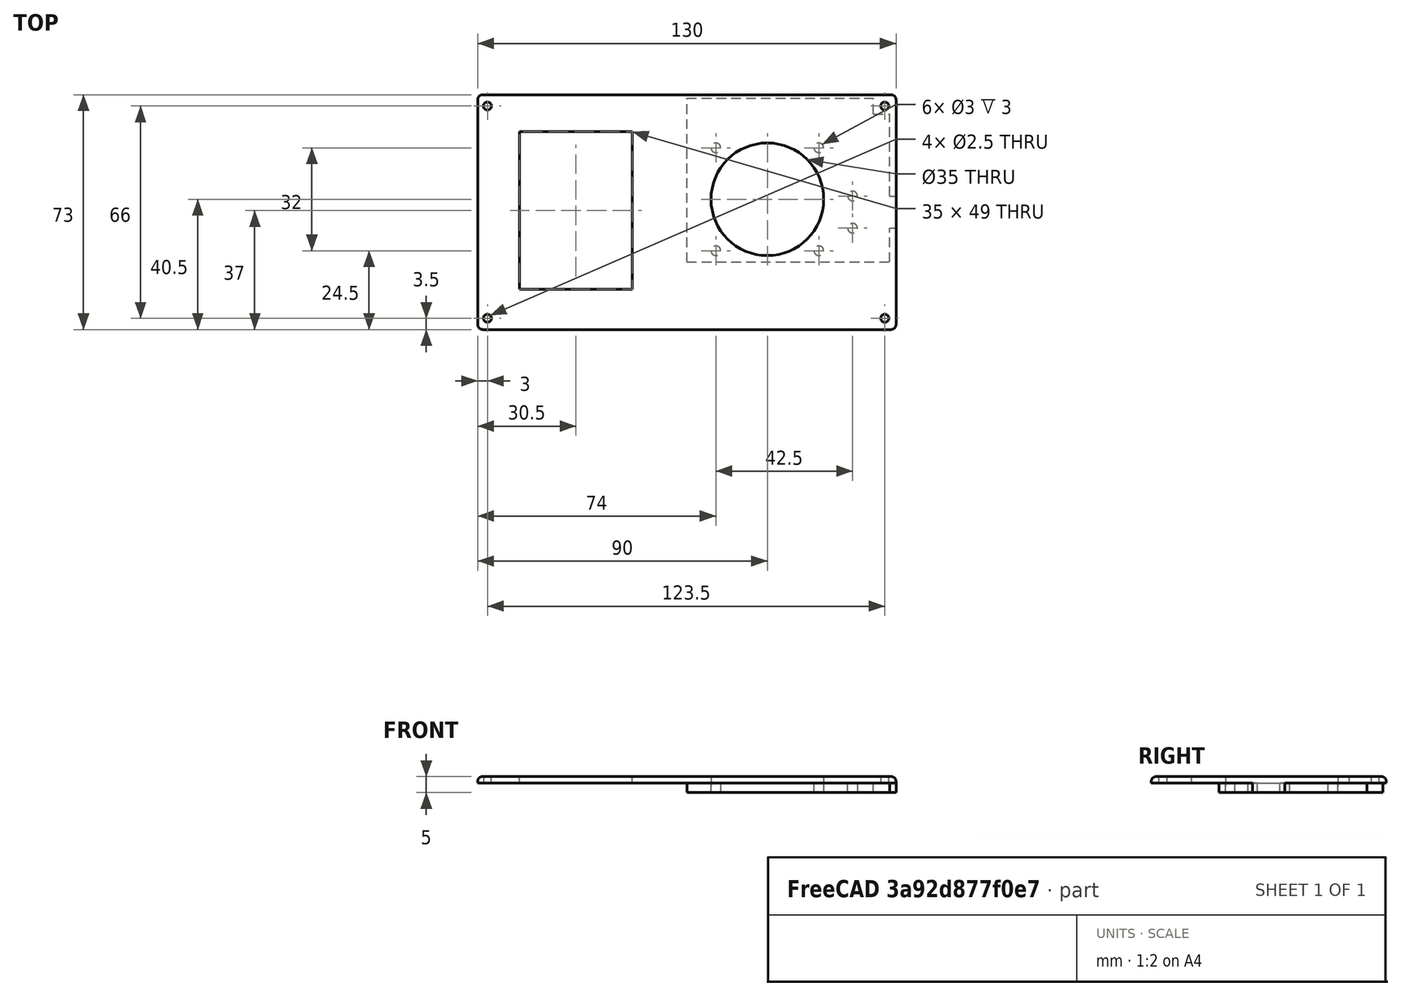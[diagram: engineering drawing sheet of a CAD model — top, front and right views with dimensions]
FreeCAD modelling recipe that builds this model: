
FCSTD DOCUMENT  (FreeCAD 1.0R39285 (Git))
Label: caseTop
License: All rights reserved
LicenseURL: https://en.wikipedia.org/wiki/All_rights_reserved
objects: PartDesign::SubtractiveCylinder×12, PartDesign::Fillet×4, PartDesign::AdditiveBox×3, PartDesign::SubtractiveBox×2, PartDesign::Body×1
note: 64 computed .brp shape members not serialized (recipe doc carries the construction recipe); baked Part::Feature solids carry a one-line shape summary decoded from their .brp

FEATURE [PartDesign::AdditiveBox] Box  label="base"
  AttacherType = Attacher::AttachEngine3D
  Height = 2
  Length = 130
  Refine = true
  Suppressed = false
  Width = 73
FEATURE [PartDesign::SubtractiveBox] Box001  label="screen"
  AttacherType = Attacher::AttachEngine3D
  AttachmentOffset = pos=(13,12.5,-4) rot=(0,0,1;0rad)
  AttachmentSupport = -> [Box]
  BaseFeature = -> Box
  Height = 4
  Length = 35
  MapMode = 5
  Placement = pos=(13,12.5,-2) rot=(0,0,1;0rad)
  Refine = true
  Suppressed = false
  Width = 49
FEATURE [PartDesign::SubtractiveCylinder] Cylinder  label="clickwheel"
  Angle = 360
  AttacherType = Attacher::AttachEngine3D
  AttachmentOffset = pos=(77,28,-8) rot=(0,0,1;0rad)
  AttachmentSupport = -> [Box001]
  BaseFeature = -> Box001
  FirstAngle = 0
  Height = 14
  MapMode = 5
  Placement = pos=(90,40.5,-6) rot=(0,0,1;0rad)
  Radius = 17.5
  Refine = true
  SecondAngle = 0
  Suppressed = false
FEATURE [PartDesign::AdditiveBox] Box002  label="clickwheelExtraBase"
  AttacherType = Attacher::AttachEngine3D
  AttachmentOffset = pos=(-25,-19.5,-5) rot=(0,0,1;0rad)
  AttachmentSupport = -> [Cylinder]
  BaseFeature = -> Cylinder
  Height = 3
  Length = 63
  MapMode = 5
  Placement = pos=(65,21,-3) rot=(0,0,1;0rad)
  Refine = true
  Suppressed = false
  Width = 51
FEATURE [PartDesign::SubtractiveCylinder] Cylinder001  label="clickwheelExtended"
  Angle = 360
  AttacherType = Attacher::AttachEngine3D
  AttachmentOffset = pos=(25,19.5,-5) rot=(0,0,1;0rad)
  AttachmentSupport = -> [Box002]
  BaseFeature = -> Box002
  FirstAngle = 0
  Height = 10
  MapMode = 5
  Placement = pos=(90,40.5,-5) rot=(0,0,1;0rad)
  Radius = 17.5
  Refine = true
  SecondAngle = 0
  Suppressed = false
FEATURE [PartDesign::SubtractiveCylinder] Cylinder002  label="clickwheelMountHollow1"
  Angle = 360
  AttacherType = Attacher::AttachEngine3D
  AttachmentOffset = pos=(16,16,-3) rot=(0,0,1;0rad)
  AttachmentSupport = -> [Cylinder001]
  BaseFeature = -> Cylinder001
  FirstAngle = 0
  Height = 3
  MapMode = 5
  Placement = pos=(106,24.5,0) rot=(1,0,0;3.14159rad)
  Radius = 1.5
  Refine = true
  SecondAngle = 0
  Suppressed = false
FEATURE [PartDesign::SubtractiveCylinder] Cylinder003  label="clickwheelMountHollow2"
  Angle = 360
  AttacherType = Attacher::AttachEngine3D
  AttachmentOffset = pos=(-32,0,-3) rot=(0,0,1;0rad)
  AttachmentSupport = -> [Cylinder002]
  BaseFeature = -> Cylinder002
  FirstAngle = 0
  Height = 3
  MapMode = 5
  Placement = pos=(74,24.5,0) rot=(1,0,0;3.14159rad)
  Radius = 1.5
  Refine = true
  SecondAngle = 0
  Suppressed = false
FEATURE [PartDesign::SubtractiveCylinder] Cylinder004  label="clickwheelMountHollow3"
  Angle = 360
  AttacherType = Attacher::AttachEngine3D
  AttachmentOffset = pos=(0,-32,-3) rot=(0,0,1;0rad)
  AttachmentSupport = -> [Cylinder003]
  BaseFeature = -> Cylinder003
  FirstAngle = 0
  Height = 3
  MapMode = 5
  Placement = pos=(74,56.5,0) rot=(1,0,0;3.14159rad)
  Radius = 1.5
  Refine = true
  SecondAngle = 0
  Suppressed = false
FEATURE [PartDesign::SubtractiveCylinder] Cylinder005  label="clickwheelMountHollow4"
  Angle = 360
  AttacherType = Attacher::AttachEngine3D
  AttachmentOffset = pos=(32,0,-3) rot=(0,0,1;0rad)
  AttachmentSupport = -> [Cylinder004]
  BaseFeature = -> Cylinder004
  FirstAngle = 0
  Height = 3
  MapMode = 5
  Placement = pos=(106,56.5,0) rot=(1,0,0;3.14159rad)
  Radius = 1.5
  Refine = true
  SecondAngle = 0
  Suppressed = false
FEATURE [PartDesign::SubtractiveCylinder] Cylinder006  label="usbPortHollow"
  Angle = 360
  AttacherType = Attacher::AttachEngine3D
  AttachmentOffset = pos=(10.5,15,-3) rot=(0,0,1;0rad)
  AttachmentSupport = -> [Cylinder005]
  BaseFeature = -> Cylinder005
  FirstAngle = 0
  Height = 3
  MapMode = 5
  Placement = pos=(116.5,41.5,-7.1e-15) rot=(1,0,0;3.14159rad)
  Radius = 1.5
  Refine = true
  SecondAngle = 0
  Suppressed = false
FEATURE [PartDesign::SubtractiveCylinder] Cylinder007  label="usbPortHollow2"
  Angle = 360
  AttacherType = Attacher::AttachEngine3D
  AttachmentOffset = pos=(0,10,-3) rot=(0,0,1;0rad)
  AttachmentSupport = -> [Cylinder006]
  BaseFeature = -> Cylinder006
  FirstAngle = 0
  Height = 3
  MapMode = 5
  Placement = pos=(116.5,31.5,-1.51e-14) rot=(1,0,0;3.14159rad)
  Radius = 1.5
  Refine = true
  SecondAngle = 0
  Suppressed = false
FEATURE [PartDesign::AdditiveBox] Box003  label="usbPortAdd"
  AttacherType = Attacher::AttachEngine3D
  AttachmentOffset = pos=(11.5,-10,0) rot=(0,0,1;0rad)
  AttachmentSupport = -> [Cylinder007]
  BaseFeature = -> Cylinder007
  Height = 3
  Length = 2
  MapMode = 5
  Placement = pos=(128,41.5,-1.51e-14) rot=(1,0,0;3.14159rad)
  Refine = true
  Suppressed = false
  Width = 10
FEATURE [PartDesign::SubtractiveBox] Box004  label="screwMountRecess"
  AttacherType = Attacher::AttachEngine3D
  AttachmentOffset = pos=(-5,25.5,-5) rot=(0,0,1;0rad)
  AttachmentSupport = -> [Box003]
  BaseFeature = -> Box003
  Height = 3
  Length = 5
  MapMode = 5
  Placement = pos=(123,67,-3) rot=(0,0,1;0rad)
  Refine = true
  Suppressed = false
  Width = 5
FEATURE [PartDesign::SubtractiveCylinder] Cylinder008  label="screwHoleTop2"
  Angle = 360
  AttacherType = Attacher::AttachEngine3D
  AttachmentOffset = pos=(-120,2.5,-2) rot=(0,0,1;0rad)
  AttachmentSupport = -> [Box004]
  BaseFeature = -> Box004
  FirstAngle = 0
  Height = 2
  MapMode = 5
  Placement = pos=(3,69.5,-9.8e-15) rot=(0,0,1;0rad)
  Radius = 1.25
  Refine = true
  SecondAngle = 0
  Suppressed = false
FEATURE [PartDesign::SubtractiveCylinder] Cylinder009  label="screwHoleTop1"
  Angle = 360
  AttacherType = Attacher::AttachEngine3D
  AttachmentOffset = pos=(0,-66,-2) rot=(0,0,1;0rad)
  AttachmentSupport = -> [Cylinder008]
  BaseFeature = -> Cylinder008
  FirstAngle = 0
  Height = 2
  MapMode = 5
  Placement = pos=(3,3.5,-9.8e-15) rot=(0,0,1;0rad)
  Radius = 1.25
  Refine = true
  SecondAngle = 0
  Suppressed = false
FEATURE [PartDesign::SubtractiveCylinder] Cylinder010  label="screwHoleBottom1"
  Angle = 360
  AttacherType = Attacher::AttachEngine3D
  AttachmentOffset = pos=(123.5,0,-2) rot=(0,0,1;0rad)
  AttachmentSupport = -> [Cylinder009]
  BaseFeature = -> Cylinder009
  FirstAngle = 0
  Height = 2
  MapMode = 5
  Placement = pos=(126.5,3.5,-9.8e-15) rot=(0,0,1;0rad)
  Radius = 1.25
  Refine = true
  SecondAngle = 0
  Suppressed = false
FEATURE [PartDesign::SubtractiveCylinder] Cylinder011  label="screwHoleBottom2"
  Angle = 360
  AttacherType = Attacher::AttachEngine3D
  AttachmentOffset = pos=(0,66,-2) rot=(0,0,1;0rad)
  AttachmentSupport = -> [Cylinder010]
  BaseFeature = -> Cylinder010
  FirstAngle = 0
  Height = 2
  MapMode = 5
  Placement = pos=(126.5,69.5,-9.8e-15) rot=(0,0,1;0rad)
  Radius = 1.25
  Refine = true
  SecondAngle = 0
  Suppressed = false
FEATURE [PartDesign::Fillet] Fillet
  Base = -> Cylinder011 [Edge7]
  BaseFeature = -> Cylinder011
  Placement = pos=(126.5,69.5,-9.8e-15) rot=(0,0,1;0rad)
  Radius = 1.5
  Refine = true
  SupportTransform = false
  Suppressed = false
  UseAllEdges = false
FEATURE [PartDesign::Fillet] Fillet001
  Base = -> Fillet [Edge32]
  BaseFeature = -> Fillet
  Placement = pos=(126.5,69.5,-9.8e-15) rot=(0,0,1;0rad)
  Radius = 1.5
  Refine = true
  SupportTransform = false
  Suppressed = false
  UseAllEdges = false
FEATURE [PartDesign::Fillet] Fillet002
  Base = -> Fillet001 [Edge37]
  BaseFeature = -> Fillet001
  Placement = pos=(126.5,69.5,-9.8e-15) rot=(0,0,1;0rad)
  Radius = 1.5
  Refine = true
  SupportTransform = false
  Suppressed = false
  UseAllEdges = false
FEATURE [PartDesign::Fillet] Fillet003
  Base = -> Fillet002 [Edge1]
  BaseFeature = -> Fillet002
  Placement = pos=(126.5,69.5,-9.8e-15) rot=(0,0,1;0rad)
  Radius = 1.5
  Refine = true
  SupportTransform = false
  Suppressed = false
  UseAllEdges = false
FEATURE [PartDesign::Body] Body
  AllowCompound = false
  Group = -> [Box,Box001,Cylinder,Box002,Cylinder001,Cylinder002,Cylinder003,Cylinder004,Cylinder005,Cylinder006,Cylinder007,Box003,Box004,Cylinder008,Cylinder009,Cylinder010,Cylinder011,Fillet,Fillet001,Fillet002,Fillet003]
  Origin = -> Origin
  Tip = -> Fillet003
